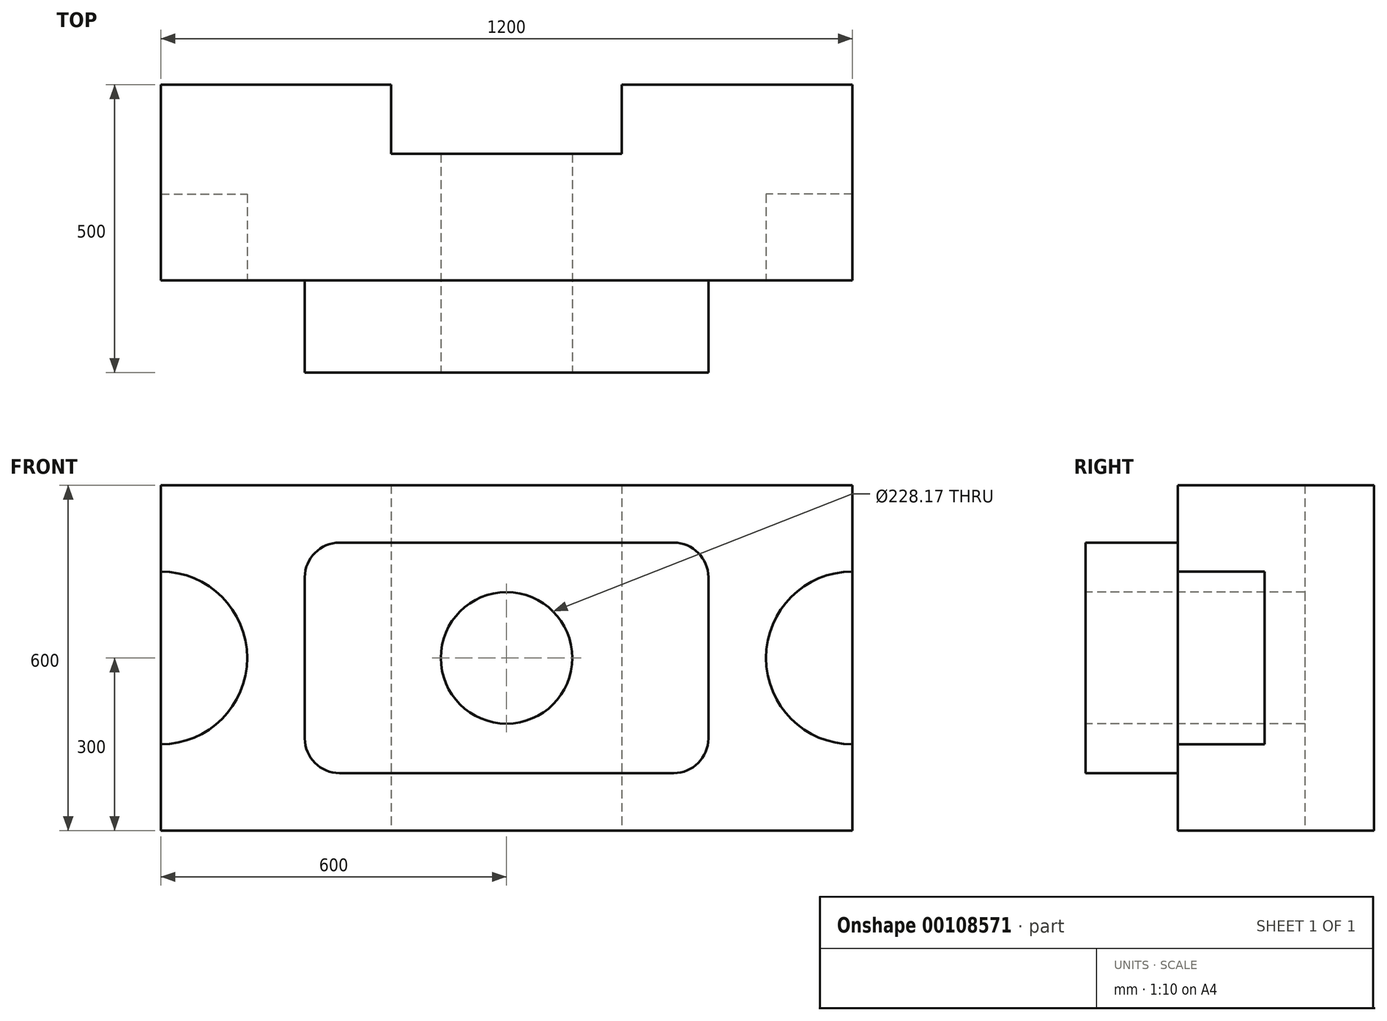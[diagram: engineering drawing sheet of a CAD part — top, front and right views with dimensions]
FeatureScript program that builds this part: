
annotation { "Feature Type Name" : "Feature", "Feature Type Description" : "" }
export const myFeature = defineFeature(function(context is Context, id is Id, definition is map)
    precondition{}
    {
        {
            var Q0;
            Q0=qCreatedBy(makeId("Front.planeOp"),FACE);
            var sketch = newSketch(context, id + "F0", { "sketchPlane" : qUnion([Q0])});
            skLineSegment(sketch, "E0.bottom", {"start": v(-600, -300) * mm, "end": v(600, -300) * mm});
            skLineSegment(sketch, "E0.top", {"start": v(-600, 300) * mm, "end": v(600, 300) * mm});
            skLineSegment(sketch, "E0.left", {"start": v(-600, -300) * mm, "end": v(-600, 300) * mm});
            skLineSegment(sketch, "E0.right", {"start": v(600, -300) * mm, "end": v(600, 300) * mm});
            skPoint(sketch, "E0.middle", {"position": v(0, 0) * mm});
            skSolve(sketch);
        }
        {
            var Q0;
            Q0 = qSketchRegion(id + "F0", true);
            var Q1;
            Q1=makeQuery(id+"F0.imprint","IMPRINT",FACE,{"disambiguationData":[TD([[makeQuery(id+"F0.imprint","IMPRINT",EDGE,{"derivedFrom":sQuery(id+"F0.wireOp",EDGE,"E0.bottom")}),1.0]])]});
            extrude(context, id + "F1", {"entities" : qUnion([Q0, Q1]), "depth" : 340 * mm});
        }
        {
            var Q0;
            Q0=makeQuery(id+"F1.opExtrude","CAP_FACE",FACE,{"disambiguationData":[OSD([sQuery(id+"F0.wireOp",EDGE,"E0.bottom"),sQuery(id+"F0.wireOp",EDGE,"E0.top"),sQuery(id+"F0.wireOp",EDGE,"E0.left"),sQuery(id+"F0.wireOp",EDGE,"E0.right")])],"isStart":false});
            var sketch = newSketch(context, id + "F2", { "sketchPlane" : qUnion([Q0])});
            skCircle(sketch, "E1", {"center": v(-600, 0) * mm, "radius": 150 * mm});
            skCircle(sketch, "E2", {"center": v(600, 0) * mm, "radius": 150 * mm});
            skSolve(sketch);
        }
        {
            var Q0;
            Q0 = qSketchRegion(id + "F2", true);
            extrude(context, id + "F3", {"entities" : qUnion([Q0]), "operationType" : NewBodyOperationType.REMOVE, "oppositeDirection" : true, "depth" : 150 * mm});
        }
        {
            var Q0;
            Q0=makeQuery(id+"F1.opExtrude","SWEPT_FACE",FACE,{"disambiguationData":[OSD([sQuery(id+"F0.wireOp",EDGE,"E0.bottom")])]});
            var sketch = newSketch(context, id + "F4", { "sketchPlane" : qUnion([Q0])});
            skLineSegment(sketch, "E3.bottom", {"start": v(-200, 120) * mm, "end": v(200, 120) * mm});
            skLineSegment(sketch, "E3.top", {"start": v(-200, -120) * mm, "end": v(200, -120) * mm});
            skLineSegment(sketch, "E3.left", {"start": v(-200, 120) * mm, "end": v(-200, -120) * mm});
            skLineSegment(sketch, "E3.right", {"start": v(200, 120) * mm, "end": v(200, -120) * mm});
            skPoint(sketch, "E3.middle", {"position": v(0, 0) * mm});
            skSolve(sketch);
        }
        {
            var Q0;
            Q0 = qSketchRegion(id + "F4", true);
            extrude(context, id + "F5", {"entities" : qUnion([Q0]), "operationType" : NewBodyOperationType.REMOVE, "endBound" : BoundingType.THROUGH_ALL, "oppositeDirection" : true, "depth" : 25 * mm});
        }
        {
            var Q0;
            Q0=makeQuery(id+"F1.opExtrude","CAP_FACE",FACE,{"disambiguationData":[OSD([sQuery(id+"F0.wireOp",EDGE,"E0.bottom"),sQuery(id+"F0.wireOp",EDGE,"E0.top"),sQuery(id+"F0.wireOp",EDGE,"E0.left"),sQuery(id+"F0.wireOp",EDGE,"E0.right")])],"isStart":false});
            var sketch = newSketch(context, id + "F6", { "sketchPlane" : qUnion([Q0])});
            skLineSegment(sketch, "E4.bottom", {"start": v(-290, 200) * mm, "end": v(290, 200) * mm});
            skLineSegment(sketch, "E4.top", {"start": v(-290, -200) * mm, "end": v(290, -200) * mm});
            skLineSegment(sketch, "E4.left", {"start": v(-350, 140) * mm, "end": v(-350, -140) * mm});
            skLineSegment(sketch, "E4.right", {"start": v(350, 140) * mm, "end": v(350, -140) * mm});
            skPoint(sketch, "E4.middle", {"position": v(0, 0) * mm});
            skPoint(sketch, "E5.visualSharp", {"position": v(-350, -200) * mm});
            skArc(sketch, "E5.filletArc", {"start": v(-350, -140) * mm, "mid": v(-332.43, -182.43) * mm, "end": v(-290, -200) * mm});
            skPoint(sketch, "E6.visualSharp", {"position": v(350, -200) * mm});
            skArc(sketch, "E6.filletArc", {"start": v(290, -200) * mm, "mid": v(332.43, -182.43) * mm, "end": v(350, -140) * mm});
            skPoint(sketch, "E7.visualSharp", {"position": v(350, 200) * mm});
            skArc(sketch, "E7.filletArc", {"start": v(350, 140) * mm, "mid": v(332.43, 182.43) * mm, "end": v(290, 200) * mm});
            skPoint(sketch, "E8.visualSharp", {"position": v(-350, 200) * mm});
            skArc(sketch, "E8.filletArc", {"start": v(-290, 200) * mm, "mid": v(-332.43, 182.43) * mm, "end": v(-350, 140) * mm});
            skSolve(sketch);
        }
        {
            var Q0;
            Q0 = qSketchRegion(id + "F6", true);
            var Q1;
            Q1=makeQuery(id+"F6.imprint","IMPRINT",FACE,{"disambiguationData":[TD([[makeQuery(id+"F6.imprint","IMPRINT",EDGE,{"derivedFrom":sQuery(id+"F6.wireOp",EDGE,"E4.bottom")}),-1.0]])]});
            extrude(context, id + "F7", {"entities" : qUnion([Q0, Q1]), "operationType" : NewBodyOperationType.ADD, "depth" : 160 * mm});
        }
        {
            var Q0;
            Q0=makeQuery(id+"F7.opExtrude","CAP_FACE",FACE,{"disambiguationData":[OSD([sQuery(id+"F6.wireOp",EDGE,"E4.bottom"),sQuery(id+"F6.wireOp",EDGE,"E4.top"),sQuery(id+"F6.wireOp",EDGE,"E4.left"),sQuery(id+"F6.wireOp",EDGE,"E4.right"),sQuery(id+"F6.wireOp",EDGE,"E5.filletArc"),sQuery(id+"F6.wireOp",EDGE,"E6.filletArc"),sQuery(id+"F6.wireOp",EDGE,"E7.filletArc"),sQuery(id+"F6.wireOp",EDGE,"E8.filletArc")])],"isStart":false});
            var sketch = newSketch(context, id + "F8", { "sketchPlane" : qUnion([Q0])});
            skCircle(sketch, "E9", {"center": v(0, 0) * mm, "radius": 114.08 * mm});
            skSolve(sketch);
        }
        {
            var Q0;
            Q0=makeQuery(id+"F8.imprint","IMPRINT",FACE,{"disambiguationData":[TD([[makeQuery(id+"F8.imprint","IMPRINT",EDGE,{"derivedFrom":sQuery(id+"F8.wireOp",EDGE,"E9")}),1.0]])]});
            extrude(context, id + "F9", {"entities" : qUnion([Q0]), "operationType" : NewBodyOperationType.REMOVE, "endBound" : BoundingType.THROUGH_ALL, "oppositeDirection" : true, "depth" : 25 * mm});
        }
    });
